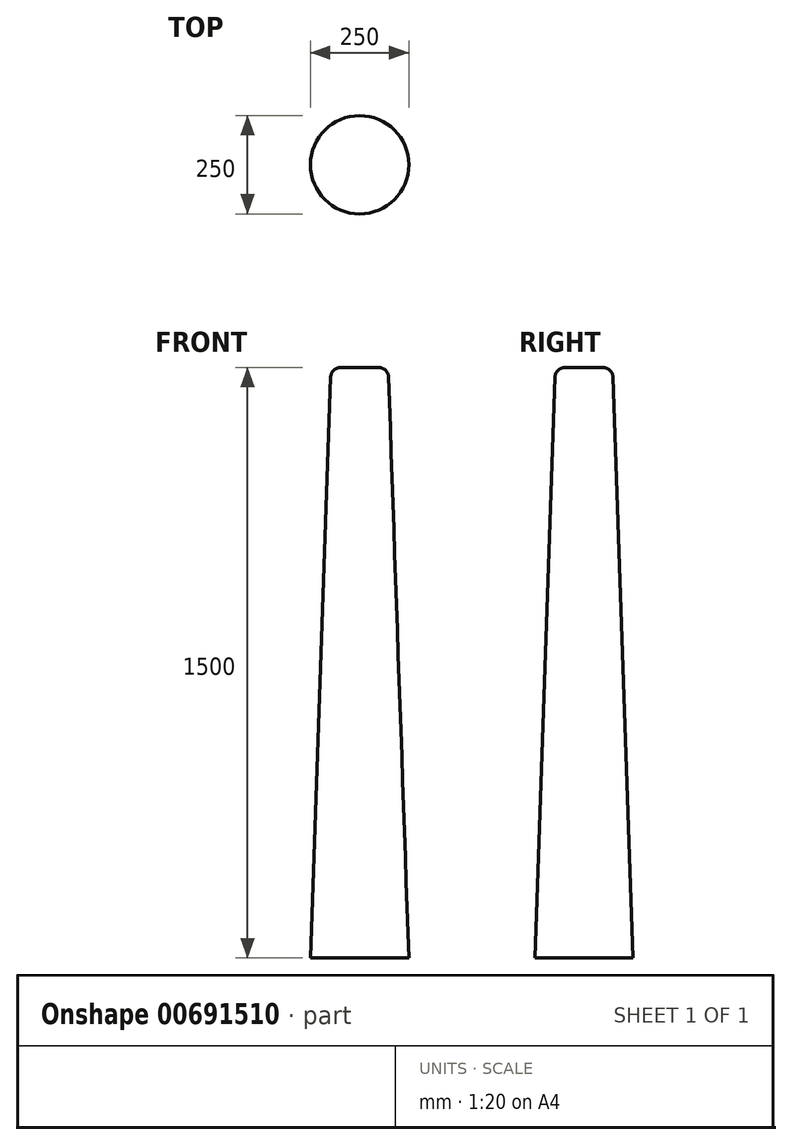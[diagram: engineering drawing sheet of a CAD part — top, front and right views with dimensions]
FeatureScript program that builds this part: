
annotation { "Feature Type Name" : "Feature", "Feature Type Description" : "" }
export const myFeature = defineFeature(function(context is Context, id is Id, definition is map)
    precondition{}
    {
        {
            var Q0;
            Q0=qCreatedBy(makeId("Top.planeOp"),FACE);
            var sketch = newSketch(context, id + "F0", { "sketchPlane" : qUnion([Q0])});
            skCircle(sketch, "E0", {"center": v(0, 0) * mm, "radius": 125 * mm});
            skSolve(sketch);
        }
        {
            var Q0;
            Q0 = qSketchRegion(id + "F0", true);
            extrude(context, id + "F1", {"entities" : qUnion([Q0]), "depth" : 1500 * mm, "offsetDistance" : 25 * mm, "hasDraft" : true, "draftAngle" : 2 * degree, "draftPullDirection" : true});
        }
        {
            var Q0;
            Q0=makeQuery(id+"F1.opExtrude","CAP_EDGE",EDGE,{"disambiguationData":[OSD([sQuery(id+"F0.wireOp",EDGE,"E0")])],"isStart":false});
            fillet(context, id + "F2", {"entities" : qUnion([Q0]), "radius" : 25 * mm, "tangentPropagation" : true, "allowEdgeOverflow" : false});
        }
    });
